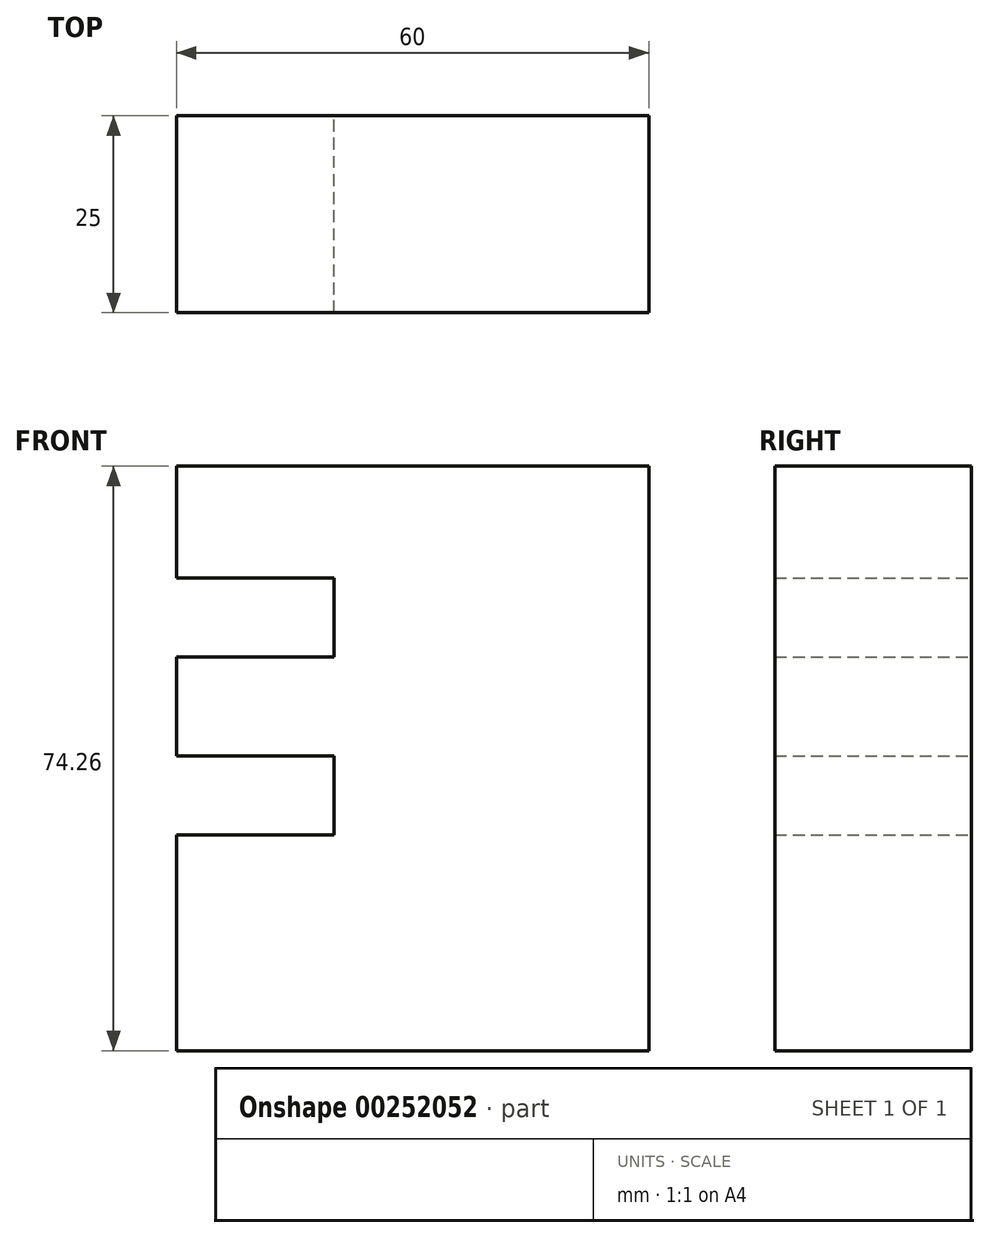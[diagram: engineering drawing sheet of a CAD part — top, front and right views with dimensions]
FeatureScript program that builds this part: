
annotation { "Feature Type Name" : "Feature", "Feature Type Description" : "" }
export const myFeature = defineFeature(function(context is Context, id is Id, definition is map)
    precondition{}
    {
        {
            var Q0;
            Q0=qCreatedBy(makeId("Front.planeOp"),FACE);
            var sketch = newSketch(context, id + "F0", { "sketchPlane" : qUnion([Q0])});
            skLineSegment(sketch, "E0.bottom", {"start": v(-30, 37.13) * mm, "end": v(30, 37.13) * mm});
            skLineSegment(sketch, "E0.top", {"start": v(-30, -37.13) * mm, "end": v(30, -37.13) * mm});
            skLineSegment(sketch, "E0.left", {"start": v(-30, 37.13) * mm, "end": v(-30, 22.9) * mm});
            skLineSegment(sketch, "E0.right", {"start": v(30, 37.13) * mm, "end": v(30, -37.13) * mm});
            skPoint(sketch, "E0.middle", {"position": v(0, 0) * mm});
            skLineSegment(sketch, "E1.bottom", {"start": v(-10, 12.9) * mm, "end": v(-30, 12.9) * mm});
            skLineSegment(sketch, "E1.top", {"start": v(-10, 22.9) * mm, "end": v(-30, 22.9) * mm});
            skLineSegment(sketch, "E1.left", {"start": v(-10, 12.9) * mm, "end": v(-10, 22.9) * mm});
            skLineSegment(sketch, "E2.bottom", {"start": v(-10, -9.7) * mm, "end": v(-30, -9.7) * mm});
            skLineSegment(sketch, "E2.top", {"start": v(-10, 0.3) * mm, "end": v(-30, 0.3) * mm});
            skLineSegment(sketch, "E2.left", {"start": v(-10, -9.7) * mm, "end": v(-10, 0.3) * mm});
            skLineSegment(sketch, "E3.trimOffspring", {"start": v(-30, 12.9) * mm, "end": v(-30, 0.3) * mm});
            skLineSegment(sketch, "E4.trimOffspring", {"start": v(-30, -9.7) * mm, "end": v(-30, -37.13) * mm});
            skSolve(sketch);
        }
        {
            var Q0;
            Q0=makeQuery(id+"F0.imprint","IMPRINT",FACE,{"disambiguationData":[TD([[makeQuery(id+"F0.imprint","IMPRINT",EDGE,{"derivedFrom":sQuery(id+"F0.wireOp",EDGE,"E0.bottom")}),-1.0]])]});
            extrude(context, id + "F1", {"entities" : qUnion([Q0]), "depth" : 25 * mm});
        }
    });
